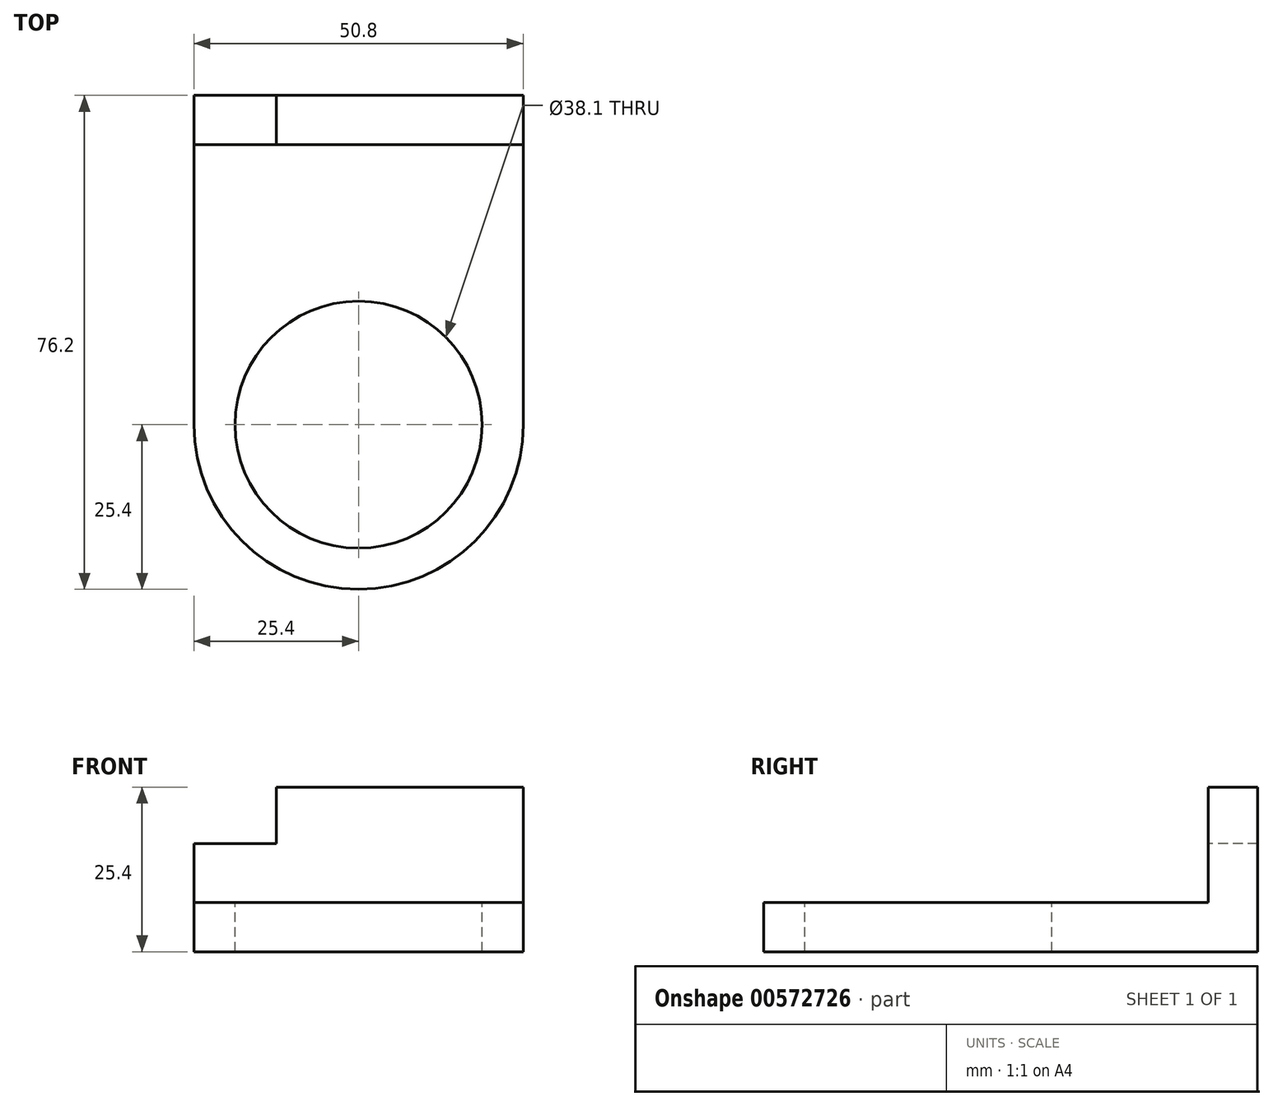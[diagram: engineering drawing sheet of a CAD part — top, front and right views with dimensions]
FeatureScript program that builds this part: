
annotation { "Feature Type Name" : "Feature", "Feature Type Description" : "" }
export const myFeature = defineFeature(function(context is Context, id is Id, definition is map)
    precondition{}
    {
        {
            var Q0;
            Q0=qCreatedBy(makeId("Top.planeOp"),FACE);
            var sketch = newSketch(context, id + "F0", { "sketchPlane" : qUnion([Q0])});
            skLineSegment(sketch, "E0.bottom", {"start": v(-25.4, 25.4) * mm, "end": v(25.4, 25.4) * mm});
            skLineSegment(sketch, "E0.left", {"start": v(-25.4, 25.4) * mm, "end": v(-25.4, -25.4) * mm});
            skLineSegment(sketch, "E0.right", {"start": v(25.4, 25.4) * mm, "end": v(25.4, -25.4) * mm});
            skArc(sketch, "E1", {"start": v(25.4, -25.4) * mm, "mid": v(0, -50.8) * mm, "end": v(-25.4, -25.4) * mm});
            skSolve(sketch);
        }
        {
            var Q0;
            Q0=makeQuery(id+"F0.imprint","IMPRINT",FACE,{"disambiguationData":[TD([[makeQuery(id+"F0.imprint","IMPRINT",EDGE,{"derivedFrom":sQuery(id+"F0.wireOp",EDGE,"E0.bottom")}),-1.0]])]});
            extrude(context, id + "F1", {"entities" : qUnion([Q0]), "depth" : 25.4 * mm, "offsetDistance" : 25.4 * mm});
        }
        {
            var Q0;
            Q0=makeQuery(id+"F1.opExtrude","SWEPT_FACE",FACE,{"disambiguationData":[OSD([sQuery(id+"F0.wireOp",EDGE,"E0.right")])]});
            var sketch = newSketch(context, id + "F2", { "sketchPlane" : qUnion([Q0])});
            skLineSegment(sketch, "E2.bottom", {"start": v(-60.67, 33.02) * mm, "end": v(17.78, 33.02) * mm});
            skLineSegment(sketch, "E2.top", {"start": v(-60.67, 7.62) * mm, "end": v(17.78, 7.62) * mm});
            skLineSegment(sketch, "E2.left", {"start": v(-60.67, 33.02) * mm, "end": v(-60.67, 7.62) * mm});
            skLineSegment(sketch, "E2.right", {"start": v(17.78, 33.02) * mm, "end": v(17.78, 7.62) * mm});
            skSolve(sketch);
        }
        {
            var Q0;
            {var subQ0=sQuery(id+"F2.wireOp",EDGE,"E2.right");var subQ1=sQuery(id+"F2.wireOp",EDGE,"E2.top");var subQ2=makeQuery(id+"F2.imprint","INTERSECT",VERTEX,{"derivedFrom":[subQ1,subQ0]});Q0=makeQuery(id+"F2.imprint","IMPRINT",FACE,{"disambiguationData":[TD([[makeQuery(id+"F2.imprint","IMPRINT",EDGE,{"disambiguationData":[TD([[subQ2,1.0]])],"derivedFrom":subQ0}),-1.0]])]});}
            var Q1;
            {var subQ1=sQuery(id+"F2.wireOp",EDGE,"E2.bottom");Q1=makeQuery(id+"F2.imprint","IMPRINT",FACE,{"disambiguationData":[TD([[makeQuery(id+"F2.imprint","IMPRINT",EDGE,{"derivedFrom":subQ1}),-1.0]])]});}
            var Q2;
            Q2=sQuery(id+"F2.wireOp",EDGE,"E2.left");
            extrude(context, id + "F3", {"entities" : qUnion([Q0, Q1]), "operationType" : NewBodyOperationType.REMOVE, "surfaceEntities" : qUnion([Q2]), "endBound" : BoundingType.THROUGH_ALL, "oppositeDirection" : true, "depth" : 25.4 * mm, "offsetDistance" : 25.4 * mm});
        }
        {
            var Q0;
            Q0=makeQuery(id+"F3.boolean.opBoolean","COPY",FACE,{"derivedFrom":makeQuery(id+"F3.opExtrude","SWEPT_FACE",FACE,{"disambiguationData":[OSD([sQuery(id+"F2.wireOp",EDGE,"E2.right")])]})});
            var sketch = newSketch(context, id + "F4", { "sketchPlane" : qUnion([Q0])});
            skLineSegment(sketch, "E3.bottom", {"start": v(-25.4, 25.4) * mm, "end": v(-12.7, 25.4) * mm});
            skLineSegment(sketch, "E3.top", {"start": v(-25.4, 16.66) * mm, "end": v(-12.7, 16.66) * mm});
            skLineSegment(sketch, "E3.left", {"start": v(-25.4, 25.4) * mm, "end": v(-25.4, 16.66) * mm});
            skLineSegment(sketch, "E3.right", {"start": v(-12.7, 25.4) * mm, "end": v(-12.7, 16.66) * mm});
            skSolve(sketch);
        }
        {
            var Q0;
            Q0=makeQuery(id+"F4.imprint","IMPRINT",FACE,{"disambiguationData":[TD([[makeQuery(id+"F4.imprint","IMPRINT",EDGE,{"derivedFrom":sQuery(id+"F4.wireOp",EDGE,"E3.bottom")}),-1.0]])]});
            extrude(context, id + "F5", {"entities" : qUnion([Q0]), "operationType" : NewBodyOperationType.REMOVE, "endBound" : BoundingType.THROUGH_ALL, "oppositeDirection" : true, "depth" : 25.4 * mm, "offsetDistance" : 25.4 * mm});
        }
        {
            var Q0;
            Q0=makeQuery(id+"F3.boolean.opBoolean","COPY",FACE,{"derivedFrom":makeQuery(id+"F3.opExtrude","SWEPT_FACE",FACE,{"disambiguationData":[OSD([sQuery(id+"F2.wireOp",EDGE,"E2.top")])]})});
            var sketch = newSketch(context, id + "F6", { "sketchPlane" : qUnion([Q0])});
            skCircle(sketch, "E4", {"center": v(0, -25.4) * mm, "radius": 19.05 * mm});
            skSolve(sketch);
        }
        {
            var Q0;
            Q0=makeQuery(id+"F6.imprint","IMPRINT",FACE,{"disambiguationData":[TD([[makeQuery(id+"F6.imprint","IMPRINT",EDGE,{"derivedFrom":sQuery(id+"F6.wireOp",EDGE,"E4")}),1.0]])]});
            extrude(context, id + "F7", {"entities" : qUnion([Q0]), "operationType" : NewBodyOperationType.REMOVE, "endBound" : BoundingType.THROUGH_ALL, "oppositeDirection" : true, "depth" : 25.4 * mm, "offsetDistance" : 25.4 * mm});
        }
    });
